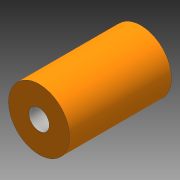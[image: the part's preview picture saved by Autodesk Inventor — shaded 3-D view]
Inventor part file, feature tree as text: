
AUTODESK INVENTOR PART (.ipt)
format: ipt  version: 2016 (Build 200138000, 138)  size: 91,648 bytes
history: native  units: mm
features: extrude x2, sketch x2
ambient origin geometry x8: Origin, YZ Plane, XZ Plane, XY Plane, X Axis, Y Axis, Z Axis, Center Point
bodies: 实体1 (feature_tree)
feature tree (4):
  extrude  "拉伸1"  Depth=15.0mm
  extrude  "拉伸3"  Depth=15.0mm TaperAngle=0.0deg
  sketch  "草图1"  dims[d0=15.0mm d1=5.0mm]
  sketch  "草图4"  dims[d2=25.0mm d3=0.0mm d12=15.0mm d13=0.0mm]
